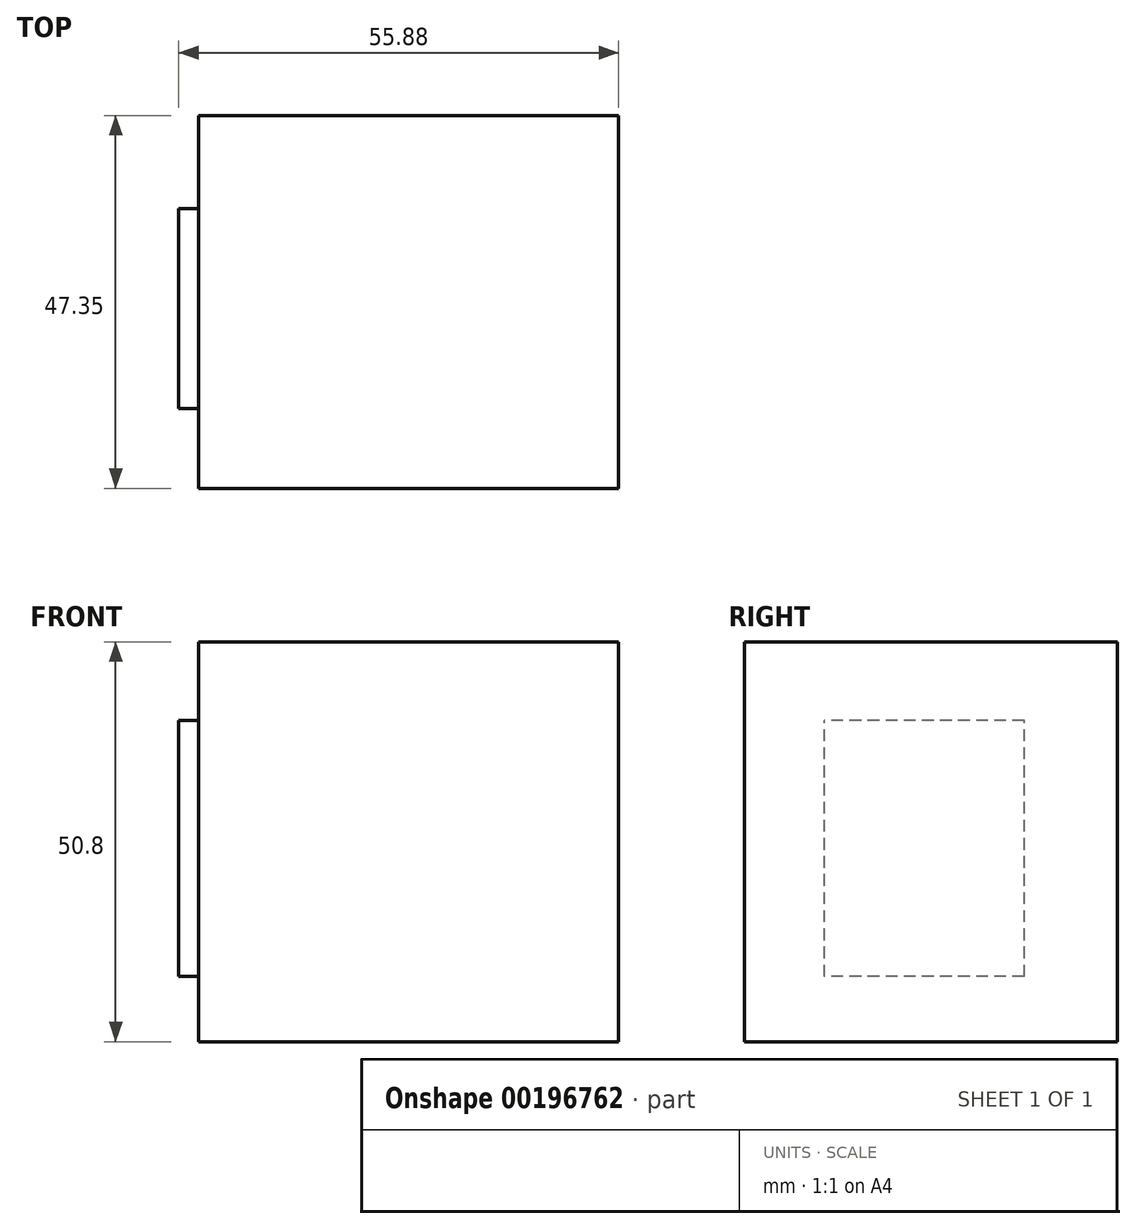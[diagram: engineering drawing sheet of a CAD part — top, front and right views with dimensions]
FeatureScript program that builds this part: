
annotation { "Feature Type Name" : "Feature", "Feature Type Description" : "" }
export const myFeature = defineFeature(function(context is Context, id is Id, definition is map)
    precondition{}
    {
        {
            var Q0;
            Q0=qCreatedBy(makeId("Top.planeOp"),FACE);
            var sketch = newSketch(context, id + "F0", { "sketchPlane" : qUnion([Q0])});
            skLineSegment(sketch, "E0.bottom", {"start": v(-25.39, 22.4) * mm, "end": v(27.95, 22.4) * mm});
            skLineSegment(sketch, "E0.top", {"start": v(-25.39, -24.96) * mm, "end": v(27.95, -24.96) * mm});
            skLineSegment(sketch, "E0.left", {"start": v(-25.39, 22.4) * mm, "end": v(-25.39, -24.96) * mm});
            skLineSegment(sketch, "E0.right", {"start": v(27.95, 22.4) * mm, "end": v(27.95, -24.96) * mm});
            skSolve(sketch);
        }
        {
            var Q0;
            Q0 = qSketchRegion(id + "F0", true);
            extrude(context, id + "F1", {"entities" : qUnion([Q0]), "oppositeDirection" : true, "depth" : 50.8 * mm});
        }
        {
            var Q0;
            Q0=makeQuery(id+"F1.opExtrude","SWEPT_FACE",FACE,{"disambiguationData":[OSD([sQuery(id+"F0.wireOp",EDGE,"E0.left")])]});
            var sketch = newSketch(context, id + "F2", { "sketchPlane" : qUnion([Q0])});
            skLineSegment(sketch, "E1.bottom", {"start": v(-10.55, -42.51) * mm, "end": v(14.85, -42.51) * mm});
            skLineSegment(sketch, "E1.top", {"start": v(-10.55, -10) * mm, "end": v(14.85, -10) * mm});
            skLineSegment(sketch, "E1.left", {"start": v(-10.55, -42.51) * mm, "end": v(-10.55, -10) * mm});
            skLineSegment(sketch, "E1.right", {"start": v(14.85, -42.51) * mm, "end": v(14.85, -10) * mm});
            skPoint(sketch, "E2.firstSnap0", {"position": v(2.15, -42.51) * mm});
            skLineSegment(sketch, "E2.bottom", {"start": v(2.15, -50.8) * mm, "end": v(0, -50.8) * mm});
            skLineSegment(sketch, "E2.top", {"start": v(2.15, -42.51) * mm, "end": v(0, -42.51) * mm});
            skLineSegment(sketch, "E2.left", {"start": v(2.15, -50.8) * mm, "end": v(2.15, -42.51) * mm});
            skLineSegment(sketch, "E2.right", {"start": v(0, -50.8) * mm, "end": v(0, -42.51) * mm});
            skSolve(sketch);
        }
        {
            var Q0;
            Q0=makeQuery(id+"F2.imprint","IMPRINT",FACE,{"disambiguationData":[TD([[makeQuery(id+"F2.imprint","IMPRINT",EDGE,{"derivedFrom":sQuery(id+"F2.wireOp",EDGE,"E1.top")}),-1.0]])]});
            extrude(context, id + "F3", {"entities" : qUnion([Q0]), "depth" : 2.54 * mm});
        }
    });
